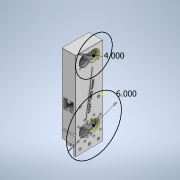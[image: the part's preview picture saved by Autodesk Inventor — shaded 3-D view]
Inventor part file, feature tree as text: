
AUTODESK INVENTOR PART (.ipt)
format: ipt  version: 2020 (Build 240168000, 168)  size: 822,784 bytes
history: native  units: in
note: dims shown in document units (in); Inventor stores cm internally (conversion verified against a paired STEP export)
features: reference x24, extrude x10, sketch x10, other x4, chamfer x1, fillet x1
ambient origin geometry x8: Origin, YZ Plane, XZ Plane, XY Plane, X Axis, Y Axis, Z Axis, Center Point
bodies: Solid1 (feature_tree)
feature tree (50):
  extrude  "Extrusion1"  Depth=5.0in
  extrude  "Extrusion2"  Depth=3.0in TaperAngle=0.0deg
  extrude  "Extrusion4"  TaperAngle=0.0deg  [1 undecoded]
  extrude  "Extrusion5"  Depth=1.126in
  extrude  "Extrusion6"  Depth=1.226in
  extrude  "Extrusion7"  Depth=1.126in
  extrude  "Extrusion8"  Depth=1.226in
  chamfer  "Chamfer3"  Distance=0.064in
  extrude  "Extrusion9"  Depth=0.165in
  fillet  "Fillet1"  [1 undecoded]
  sketch  "Sketch13"  dims[d50=1.4291in d51=0.165in d52=0.0in d53=0.0in]
  extrude  "Extrusion11"  Depth=1.0in
  extrude  "Extrusion12"  Depth=3.1496in TaperAngle=360.0deg
  reference  "Reference1"
  reference  "Reference2"
  reference  "Reference3"
  reference  "Reference4"
  reference  "Reference5"
  reference  "Reference6"
  reference  "Reference7"
  reference  "Reference8"
  reference  "Reference9"
  reference  "Reference10"
  reference  "Reference11"
  reference  "Reference12"
  reference  "Reference13"
  reference  "Reference14"
  reference  "Reference15"
  reference  "Reference16"
  reference  "Reference17"
  reference  "Reference18"
  reference  "Reference19"
  reference  "Reference20"
  reference  "Reference21"
  reference  "Reference22"
  reference  "Reference23"
  reference  "Reference24"
  sketch  "Sketch2"  dims[d0=1.5in d1=5.0in]
  sketch  "Sketch4"  dims[d2=0.2461in d3=3.0in d4=0.0in]
  sketch  "Sketch5"  dims[d7=0.2656in d24=0.0in d25=0.0in]
  sketch  "Sketch6"  dims[d31=1.023in d32=1.126in]
  sketch  "Sketch7"  dims[d33=0.314in d34=0.0in d35=1.226in]
  sketch  "Sketch8"  dims[d36=0.064in d37=0.0in d41=1.126in]
  sketch  "Sketch9"  dims[d42=0.314in d43=0.0in d44=1.226in d45=0.064in d46=0.0in]
  sketch  "Sketch14"  dims[d54=0.025in d55=0.125in d56=45.0deg d57=1.0in]
  sketch  "Sketch15"  dims[d58=0.196in d59=3.1496in d61=360.0deg d63=0.0in d64=0.0in d76=0.25in d77=4.6in d78=0.5in d79=0.5in d80=0.7874in d82=4.0in d83=1.1811in d85=1.0in d89=1.0in d90=2.0in d93=6.6939in d94=1.0in d95=1.0in d96=3.1496in d98=360.0deg d100=0.125in d101=4.0in d102=6.0in d103=0.05in d104=1.0in d105=1.0in d106=0.05in d107=0.0in d108=0.1in d109=0.05in d110=0.0in]
  other  "<userpath>\Documents\FRC\2020\ShooterPrototype.iam"
  other  "ShooterPrototype.iam"
  other  "9inSpacer:1"
  other  "1003-48-CL:4"
note: 2 required parameter values undecoded (feature->parameter linkage not recoverable at this tier; creation-order binding heuristic only, values carry confidence <= 0.55)
